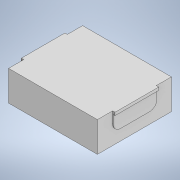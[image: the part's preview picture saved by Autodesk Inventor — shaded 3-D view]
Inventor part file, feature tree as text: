
AUTODESK INVENTOR PART (.ipt)
format: ipt  version: 2020 (Build 240168000, 168)  size: 136,192 bytes
history: native  units: mm
features: extrude x3, sketch x3, projected_geometry x2, fillet x1, mirror x1
ambient origin geometry x8: Origin, YZ Plane, XZ Plane, XY Plane, X Axis, Y Axis, Z Axis, Center Point
bodies: Solid1 (feature_tree)
feature tree (10):
  extrude  "Extrusion1"  Depth=60.96mm
  extrude  "Extrusion2"  Depth=12.7mm
  fillet  "Fillet1"  Radius=30.0mm
  extrude  "Extrusion3"  Depth=5.0mm
  mirror  "Mirror1"
  sketch  "Sketch1"  dims[d0=50.8mm d1=60.96mm]
  sketch  "Sketch2"  dims[d2=20.6629mm d3=0.0mm d4=12.7mm d5=30.0mm]
  projected_geometry  "Projected Loop1"
  sketch  "Sketch3"  dims[d6=0.5mm d7=0.0mm d8=5.0mm d9=2.0mm d10=1.17mm d11=0.0mm]
  projected_geometry  "Projected Loop2"
